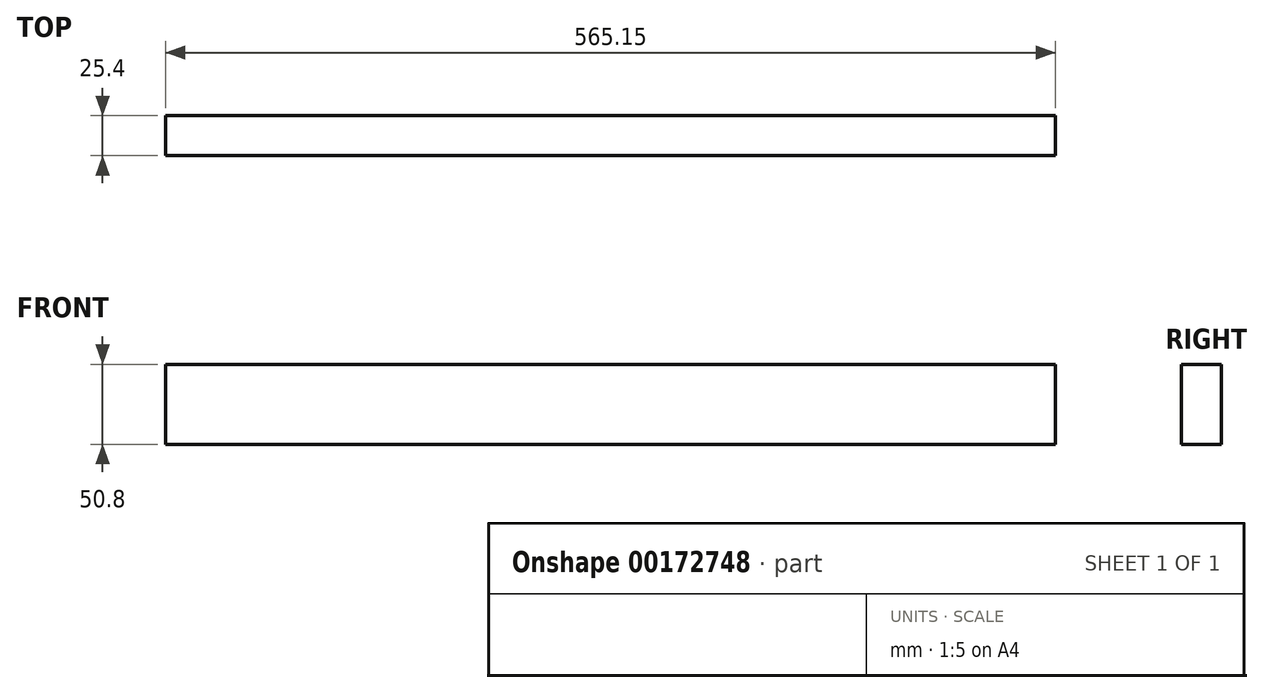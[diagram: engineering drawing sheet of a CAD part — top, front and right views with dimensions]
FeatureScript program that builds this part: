
annotation { "Feature Type Name" : "Feature", "Feature Type Description" : "" }
export const myFeature = defineFeature(function(context is Context, id is Id, definition is map)
    precondition{}
    {
        {
            var Q0;
            Q0=qCreatedBy(makeId("Front.planeOp"),FACE);
            var sketch = newSketch(context, id + "F0", { "sketchPlane" : qUnion([Q0])});
            skLineSegment(sketch, "E0.bottom", {"start": v(-158.79, 0) * mm, "end": v(406.36, 0) * mm});
            skLineSegment(sketch, "E0.top", {"start": v(-158.79, -50.8) * mm, "end": v(406.36, -50.8) * mm});
            skLineSegment(sketch, "E0.left", {"start": v(-158.79, 0) * mm, "end": v(-158.79, -50.8) * mm});
            skLineSegment(sketch, "E0.right", {"start": v(406.36, 0) * mm, "end": v(406.36, -50.8) * mm});
            skSolve(sketch);
        }
        {
            var Q0;
            Q0 = qSketchRegion(id + "F0", true);
            extrude(context, id + "F1", {"entities" : qUnion([Q0]), "depth" : 25.4 * mm});
        }
    });
